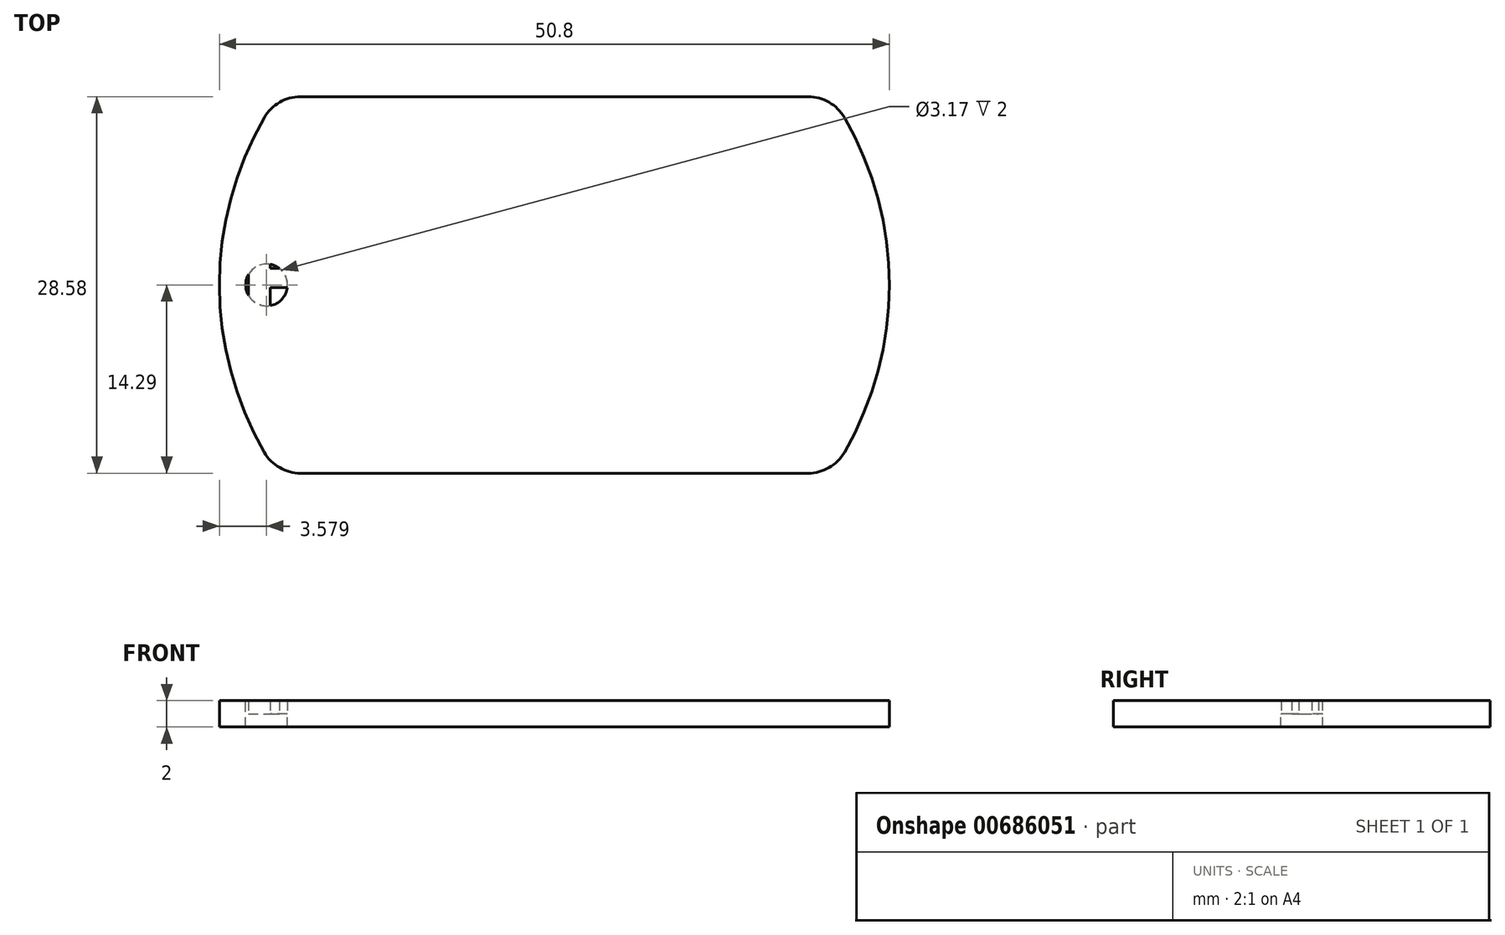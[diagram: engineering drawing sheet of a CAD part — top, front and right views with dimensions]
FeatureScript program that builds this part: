
annotation { "Feature Type Name" : "Feature", "Feature Type Description" : "" }
export const myFeature = defineFeature(function(context is Context, id is Id, definition is map)
    precondition{}
    {
        {
            var Q0;
            Q0=qCreatedBy(makeId("Top.planeOp"),FACE);
            var sketch = newSketch(context, id + "F0", { "sketchPlane" : qUnion([Q0])});
            skArc(sketch, "E0", {"start": v(-22, 12.7) * mm, "mid": v(-25.4, 0) * mm, "end": v(-22, -12.7) * mm});
            skLineSegment(sketch, "E1.top", {"start": v(-19.25, -14.29) * mm, "end": v(19.25, -14.29) * mm});
            skArc(sketch, "E2.trimOffspring", {"start": v(22, -12.7) * mm, "mid": v(25.4, 0) * mm, "end": v(22, 12.7) * mm});
            skLineSegment(sketch, "E3", {"start": v(-19.25, 14.29) * mm, "end": v(19.25, 14.29) * mm});
            skPoint(sketch, "E4.visualSharp", {"position": v(-21, 14.29) * mm});
            skArc(sketch, "E4.filletArc", {"start": v(-19.25, 14.29) * mm, "mid": v(-20.83, 13.86) * mm, "end": v(-22, 12.7) * mm});
            skPoint(sketch, "E5.visualSharp", {"position": v(21, 14.29) * mm});
            skArc(sketch, "E5.filletArc", {"start": v(22, 12.7) * mm, "mid": v(20.83, 13.86) * mm, "end": v(19.25, 14.29) * mm});
            skPoint(sketch, "E6.visualSharp", {"position": v(21, -14.29) * mm});
            skArc(sketch, "E6.filletArc", {"start": v(19.25, -14.29) * mm, "mid": v(20.83, -13.86) * mm, "end": v(22, -12.7) * mm});
            skPoint(sketch, "E7.visualSharp", {"position": v(-21, -14.29) * mm});
            skArc(sketch, "E7.filletArc", {"start": v(-22, -12.7) * mm, "mid": v(-20.83, -13.86) * mm, "end": v(-19.25, -14.29) * mm});
            skSolve(sketch);
        }
        {
            var Q0;
            Q0=makeQuery(id+"F0.imprint","IMPRINT",FACE,{"disambiguationData":[TD([[makeQuery(id+"F0.imprint","IMPRINT",EDGE,{"derivedFrom":sQuery(id+"F0.wireOp",EDGE,"E0")}),1.0]])]});
            extrude(context, id + "F1", {"entities" : qUnion([Q0]), "depth" : 1 * mm, "offsetDistance" : 25.4 * mm});
        }
        {
            var Q0;
            Q0=makeQuery(id+"F1.opExtrude","CAP_FACE",FACE,{"disambiguationData":[OSD([sQuery(id+"F0.wireOp",EDGE,"E0"),sQuery(id+"F0.wireOp",EDGE,"E1.top"),sQuery(id+"F0.wireOp",EDGE,"E2.trimOffspring"),sQuery(id+"F0.wireOp",EDGE,"E3"),sQuery(id+"F0.wireOp",EDGE,"E4.filletArc"),sQuery(id+"F0.wireOp",EDGE,"E5.filletArc"),sQuery(id+"F0.wireOp",EDGE,"E6.filletArc"),sQuery(id+"F0.wireOp",EDGE,"E7.filletArc")])],"isStart":false});
            var sketch = newSketch(context, id + "F2", { "sketchPlane" : qUnion([Q0])});
            skLineSegment(sketch, "E8.0", {"start": v(-18.66, 13.29) * mm, "end": v(18.66, 13.29) * mm});
            skArc(sketch, "E8.1", {"start": v(-21.45, 11.63) * mm, "mid": v(-24.4, 0) * mm, "end": v(-21.45, -11.63) * mm});
            skLineSegment(sketch, "E8.2", {"start": v(-18.66, -13.29) * mm, "end": v(18.66, -13.29) * mm});
            skArc(sketch, "E8.3", {"start": v(21.45, -11.63) * mm, "mid": v(24.4, 0) * mm, "end": v(21.45, 11.63) * mm});
            skPoint(sketch, "E9.visualSharp", {"position": v(-20.46, 13.29) * mm});
            skArc(sketch, "E9.filletArc", {"start": v(-18.66, 13.29) * mm, "mid": v(-20.29, 12.84) * mm, "end": v(-21.45, 11.63) * mm});
            skPoint(sketch, "E10.visualSharp", {"position": v(20.46, 13.29) * mm});
            skArc(sketch, "E10.filletArc", {"start": v(21.45, 11.63) * mm, "mid": v(20.29, 12.84) * mm, "end": v(18.66, 13.29) * mm});
            skPoint(sketch, "E11.visualSharp", {"position": v(20.46, -13.29) * mm});
            skArc(sketch, "E11.filletArc", {"start": v(18.66, -13.29) * mm, "mid": v(20.29, -12.84) * mm, "end": v(21.45, -11.63) * mm});
            skPoint(sketch, "E12.visualSharp", {"position": v(-20.46, -13.29) * mm});
            skArc(sketch, "E12.filletArc", {"start": v(-21.45, -11.63) * mm, "mid": v(-20.29, -12.84) * mm, "end": v(-18.66, -13.29) * mm});
            skLineSegment(sketch, "E13.0", {"start": v(-19.25, 14.29) * mm, "end": v(19.25, 14.29) * mm});
            skArc(sketch, "E13.1", {"start": v(-22, 12.7) * mm, "mid": v(-25.4, 0) * mm, "end": v(-22, -12.7) * mm});
            skLineSegment(sketch, "E13.2", {"start": v(-19.25, -14.29) * mm, "end": v(19.25, -14.29) * mm});
            skArc(sketch, "E13.3", {"start": v(22, -12.7) * mm, "mid": v(25.4, 0) * mm, "end": v(22, 12.7) * mm});
            skPoint(sketch, "E14.visualSharp", {"position": v(-21, -14.29) * mm});
            skArc(sketch, "E14.filletArc", {"start": v(-22, -12.7) * mm, "mid": v(-20.83, -13.86) * mm, "end": v(-19.25, -14.29) * mm});
            skPoint(sketch, "E15.visualSharp", {"position": v(21, -14.29) * mm});
            skArc(sketch, "E15.filletArc", {"start": v(19.25, -14.29) * mm, "mid": v(20.83, -13.86) * mm, "end": v(22, -12.7) * mm});
            skPoint(sketch, "E16.visualSharp", {"position": v(21, 14.29) * mm});
            skArc(sketch, "E16.filletArc", {"start": v(22, 12.7) * mm, "mid": v(20.83, 13.86) * mm, "end": v(19.25, 14.29) * mm});
            skPoint(sketch, "E17.visualSharp", {"position": v(-21, 14.29) * mm});
            skArc(sketch, "E17.filletArc", {"start": v(-19.25, 14.29) * mm, "mid": v(-20.83, 13.86) * mm, "end": v(-22, 12.7) * mm});
            skSolve(sketch);
        }
        {
            var Q0;
            Q0=makeQuery(id+"F2.imprint","IMPRINT",FACE,{"disambiguationData":[TD([[makeQuery(id+"F2.imprint","IMPRINT",EDGE,{"derivedFrom":sQuery(id+"F2.wireOp",EDGE,"E8.0")}),1.0]])]});
            extrude(context, id + "F3", {"entities" : qUnion([Q0]), "operationType" : NewBodyOperationType.ADD, "depth" : 1 * mm, "offsetDistance" : 25.4 * mm});
        }
        {
            var Q0;
            Q0=makeQuery(id+"F1.opExtrude","CAP_FACE",FACE,{"disambiguationData":[OSD([sQuery(id+"F0.wireOp",EDGE,"E0"),sQuery(id+"F0.wireOp",EDGE,"E1.top"),sQuery(id+"F0.wireOp",EDGE,"E2.trimOffspring"),sQuery(id+"F0.wireOp",EDGE,"E3"),sQuery(id+"F0.wireOp",EDGE,"E4.filletArc"),sQuery(id+"F0.wireOp",EDGE,"E5.filletArc"),sQuery(id+"F0.wireOp",EDGE,"E6.filletArc"),sQuery(id+"F0.wireOp",EDGE,"E7.filletArc")])],"isStart":false});
            var sketch = newSketch(context, id + "F4", { "sketchPlane" : qUnion([Q0])});
            skCircle(sketch, "E18", {"center": v(-21.82, 0) * mm, "radius": 1.59 * mm});
            skSolve(sketch);
        }
        {
            var Q0;
            Q0=makeQuery(id+"F4.imprint","IMPRINT",FACE,{"disambiguationData":[TD([[makeQuery(id+"F4.imprint","IMPRINT",EDGE,{"derivedFrom":sQuery(id+"F4.wireOp",EDGE,"E18")}),1.0]])]});
            extrude(context, id + "F5", {"entities" : qUnion([Q0]), "operationType" : NewBodyOperationType.REMOVE, "oppositeDirection" : true, "depth" : 1 * mm, "offsetDistance" : 25.4 * mm});
        }
        {
            var Q0;
            Q0=makeQuery(id+"F1.opExtrude","CAP_FACE",FACE,{"disambiguationData":[OSD([sQuery(id+"F0.wireOp",EDGE,"E0"),sQuery(id+"F0.wireOp",EDGE,"E1.top"),sQuery(id+"F0.wireOp",EDGE,"E2.trimOffspring"),sQuery(id+"F0.wireOp",EDGE,"E3"),sQuery(id+"F0.wireOp",EDGE,"E4.filletArc"),sQuery(id+"F0.wireOp",EDGE,"E5.filletArc"),sQuery(id+"F0.wireOp",EDGE,"E6.filletArc"),sQuery(id+"F0.wireOp",EDGE,"E7.filletArc")])],"isStart":false});
            var sketch = newSketch(context, id + "F6", { "sketchPlane" : qUnion([Q0])});
            skText(sketch, "E19", { "text": "Fines", "fontName": "OpenSans-Regular.ttf"});
            const initialGuessF6  = {"E19": [-0.02517, -0.00631, 1, 0, 0.0144]};
            skSetInitialGuess(sketch, initialGuessF6);
            skSolve(sketch);
        }
        {
            var Q0;
            Q0 = qSketchRegion(id + "F6", true);
            extrude(context, id + "F7", {"entities" : qUnion([Q0]), "operationType" : NewBodyOperationType.ADD, "depth" : 1 * mm, "offsetDistance" : 25.4 * mm});
        }
        {
            var Q0;
            Q0=makeQuery(id+"F1.opExtrude","CAP_FACE",FACE,{"disambiguationData":[OSD([sQuery(id+"F0.wireOp",EDGE,"E0"),sQuery(id+"F0.wireOp",EDGE,"E1.top"),sQuery(id+"F0.wireOp",EDGE,"E2.trimOffspring"),sQuery(id+"F0.wireOp",EDGE,"E3"),sQuery(id+"F0.wireOp",EDGE,"E4.filletArc"),sQuery(id+"F0.wireOp",EDGE,"E5.filletArc"),sQuery(id+"F0.wireOp",EDGE,"E6.filletArc"),sQuery(id+"F0.wireOp",EDGE,"E7.filletArc")])],"isStart":false});
            extrude(context, id + "F8", {"entities" : qUnion([Q0]), "operationType" : NewBodyOperationType.ADD, "depth" : 1 * mm, "offsetDistance" : 25.4 * mm});
        }
    });
